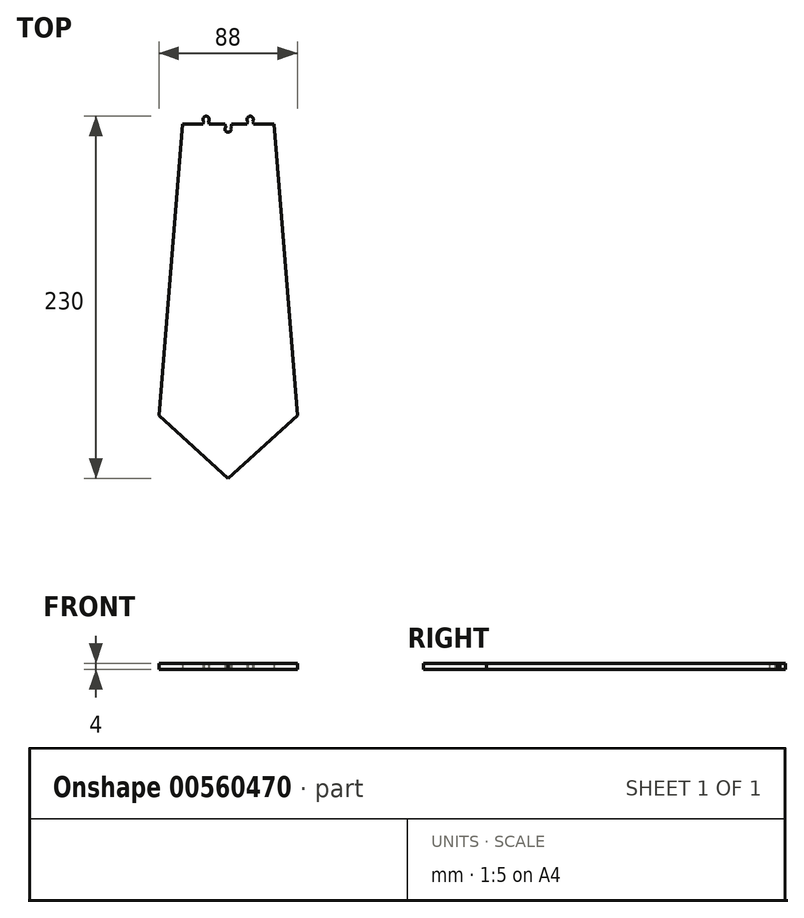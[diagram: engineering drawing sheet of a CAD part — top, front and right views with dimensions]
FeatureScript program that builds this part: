
annotation { "Feature Type Name" : "Feature", "Feature Type Description" : "" }
export const myFeature = defineFeature(function(context is Context, id is Id, definition is map)
    precondition{}
    {
        {
            var Q0;
            Q0=qCreatedBy(makeId("Top.planeOp"),FACE);
            var sketch = newSketch(context, id + "F0", { "sketchPlane" : qUnion([Q0])});
            skLineSegment(sketch, "E0", {"start": v(-1.09, 100.04) * mm, "end": v(-1.09, 94.88) * mm});
            skLineSegment(sketch, "E1", {"start": v(0.91, 100.04) * mm, "end": v(27.91, 100.04) * mm});
            skLineSegment(sketch, "E2", {"start": v(27.91, 100.04) * mm, "end": v(14.91, 100.04) * mm});
            skPoint(sketch, "E3", {"position": v(-15.09, 100.04) * mm});
            skPoint(sketch, "E4", {"position": v(-1.09, 100.04) * mm});
            skPoint(sketch, "E5", {"position": v(12.91, 100.04) * mm});
            skLineSegment(sketch, "E6", {"start": v(-17.09, 100.04) * mm, "end": v(-17.09, 101.04) * mm});
            skLineSegment(sketch, "E7", {"start": v(-13.09, 100.04) * mm, "end": v(-13.09, 101.04) * mm});
            skLineSegment(sketch, "E8", {"start": v(-3.09, 100.04) * mm, "end": v(-3.09, 99.04) * mm});
            skLineSegment(sketch, "E9", {"start": v(0.91, 100.04) * mm, "end": v(0.91, 98.88) * mm});
            skLineSegment(sketch, "E10", {"start": v(14.91, 100.04) * mm, "end": v(14.91, 101.04) * mm});
            skLineSegment(sketch, "E11", {"start": v(10.91, 100.04) * mm, "end": v(10.91, 101.04) * mm});
            skPoint(sketch, "E12", {"position": v(-1.09, 94.88) * mm});
            skArc(sketch, "E13", {"start": v(-2.42, 98.37) * mm, "mid": v(-1.14, 94.88) * mm, "end": v(0.33, 98.3) * mm});
            skLineSegment(sketch, "E14", {"start": v(-3.09, 99.04) * mm, "end": v(-2.42, 98.37) * mm});
            skPoint(sketch, "E15", {"position": v(12.91, 104.88) * mm});
            skArc(sketch, "E16", {"start": v(14.33, 101.63) * mm, "mid": v(12.91, 105.04) * mm, "end": v(11.5, 101.63) * mm});
            skLineSegment(sketch, "E17", {"start": v(10.91, 101.04) * mm, "end": v(11.5, 101.63) * mm});
            skArc(sketch, "E18", {"start": v(-13.67, 101.63) * mm, "mid": v(-15.09, 105.04) * mm, "end": v(-16.5, 101.63) * mm});
            skLineSegment(sketch, "E19", {"start": v(-13.09, 101.04) * mm, "end": v(-13.67, 101.63) * mm});
            skLineSegment(sketch, "E20", {"start": v(-17.09, 101.04) * mm, "end": v(-16.5, 101.63) * mm});
            skLineSegment(sketch, "E21.trimOffspring", {"start": v(-3.09, 100.04) * mm, "end": v(-13.09, 100.04) * mm});
            skLineSegment(sketch, "E22.trimOffspring", {"start": v(0.33, 98.3) * mm, "end": v(0.91, 98.88) * mm});
            skLineSegment(sketch, "E23.trimOffspring", {"start": v(14.33, 101.63) * mm, "end": v(14.91, 101.04) * mm});
            skLineSegment(sketch, "E24.trimOffspring", {"start": v(10.91, 100.04) * mm, "end": v(0.91, 100.04) * mm});
            skLineSegment(sketch, "E25.trimOffspring", {"start": v(-17.09, 100.04) * mm, "end": v(-30.09, 100.04) * mm});
            skPoint(sketch, "E26", {"position": v(-1.09, -84.96) * mm});
            skLineSegment(sketch, "E27", {"start": v(42.91, -84.96) * mm, "end": v(-1.09, -124.96) * mm});
            skLineSegment(sketch, "E28", {"start": v(-1.09, -124.96) * mm, "end": v(-45.09, -84.96) * mm});
            skLineSegment(sketch, "E29", {"start": v(-45.09, -84.96) * mm, "end": v(-30.09, 100.04) * mm});
            skLineSegment(sketch, "E30", {"start": v(27.91, 100.04) * mm, "end": v(42.91, -84.96) * mm});
            skSolve(sketch);
        }
        {
            var Q0;
            Q0=qSketchRegion(id+"F0",true);
            extrude(context, id + "F1", {"entities" : qUnion([Q0]), "depth" : 4 * mm, "offsetDistance" : 25 * mm});
        }
    });
